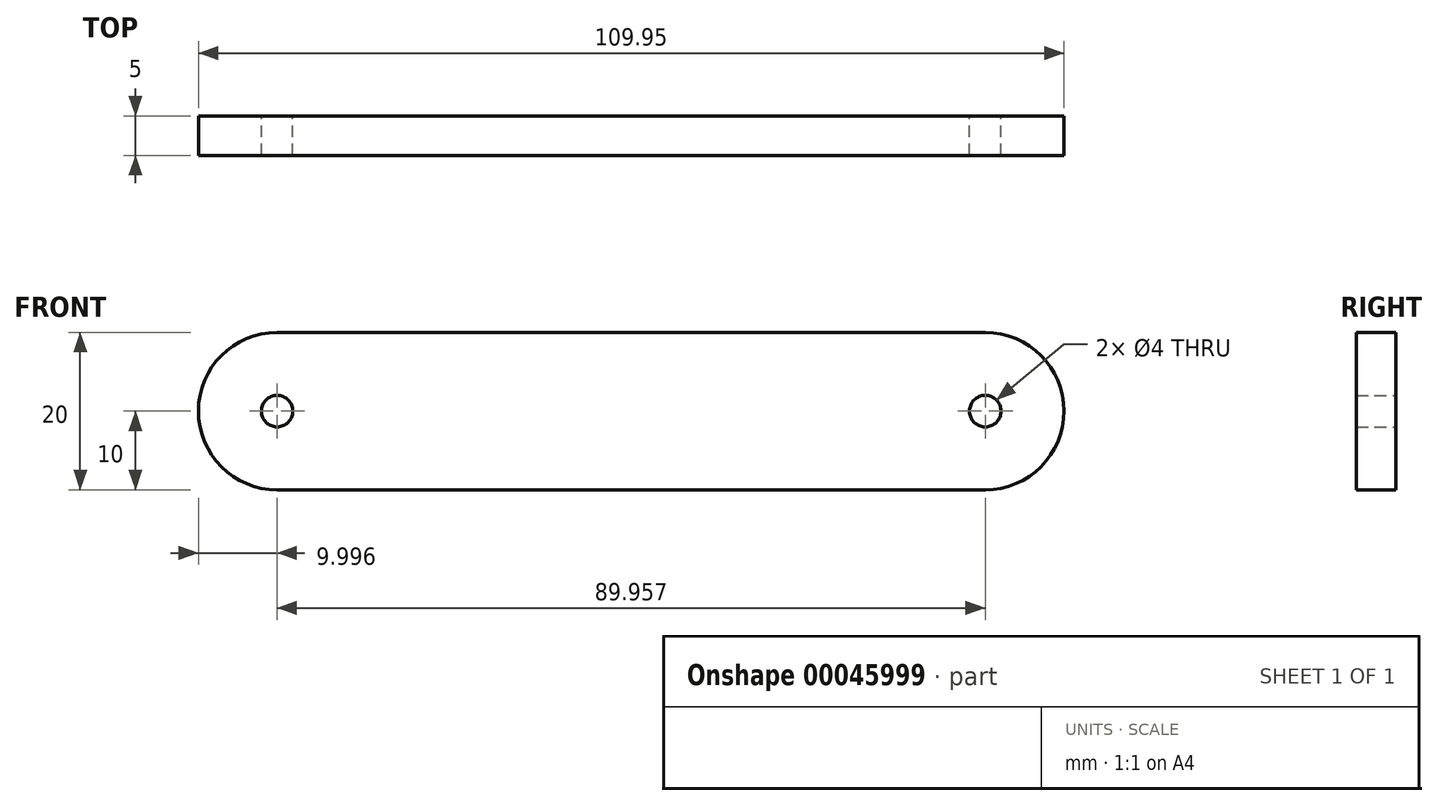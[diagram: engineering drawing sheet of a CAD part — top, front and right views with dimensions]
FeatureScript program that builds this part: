
annotation { "Feature Type Name" : "Feature", "Feature Type Description" : "" }
export const myFeature = defineFeature(function(context is Context, id is Id, definition is map)
    precondition{}
    {
        {
            var Q0;
            Q0=qCreatedBy(makeId("Front.planeOp"),FACE);
            var sketch = newSketch(context, id + "F0", { "sketchPlane" : qUnion([Q0])});
            skPoint(sketch, "E0", {"position": v(-71.37, 0) * mm});
            skPoint(sketch, "E1", {"position": v(18.58, 0) * mm});
            skCircle(sketch, "E2", {"center": v(-71.37, 0) * mm, "radius": 2 * mm});
            skCircle(sketch, "E3", {"center": v(18.58, 0) * mm, "radius": 2 * mm});
            skArc(sketch, "E4", {"start": v(-71.37, 10) * mm, "mid": v(-81.37, 0) * mm, "end": v(-71.37, -10) * mm});
            skArc(sketch, "E5", {"start": v(18.58, 10) * mm, "mid": v(28.58, 0) * mm, "end": v(18.58, -10) * mm});
            skLineSegment(sketch, "E6", {"start": v(-71.37, 10) * mm, "end": v(18.58, 10) * mm});
            skLineSegment(sketch, "E7", {"start": v(18.58, -10) * mm, "end": v(-71.37, -10) * mm});
            skLineSegment(sketch, "E8", {"start": v(-71.37, 0) * mm, "end": v(18.58, 0) * mm, "construction": true});
            skSolve(sketch);
        }
        {
            var Q0;
            Q0=qSketchRegion(id+"F0",true);
            extrude(context, id + "F1", {"entities" : qUnion([Q0]), "depth" : 5 * mm});
        }
    });
